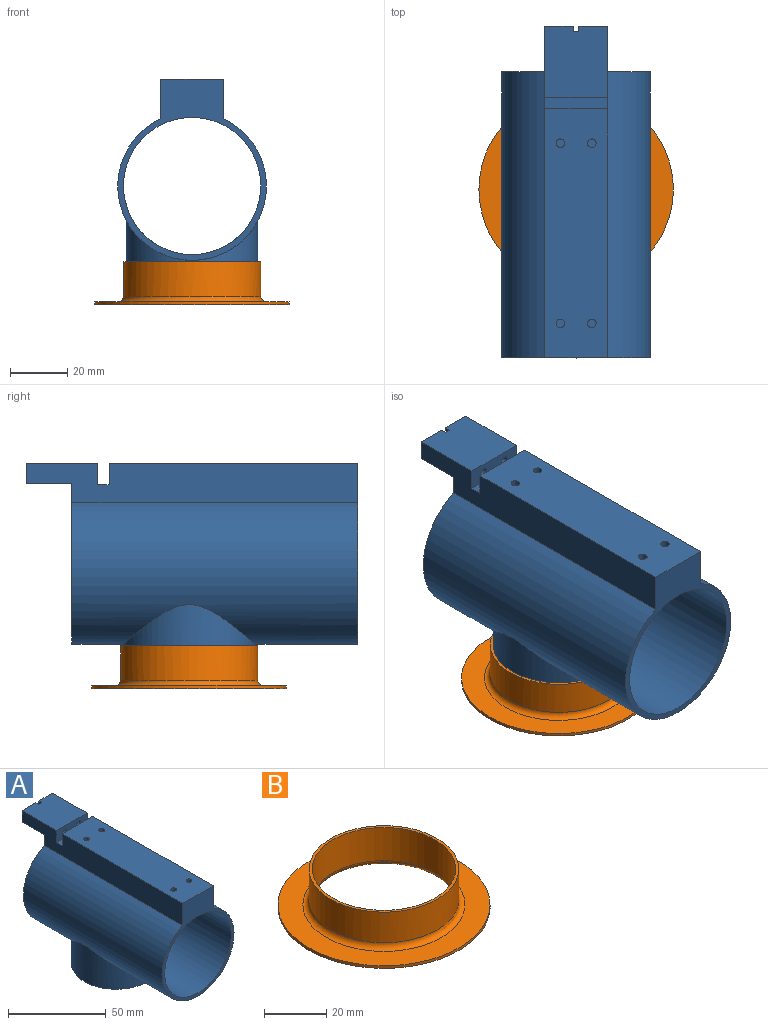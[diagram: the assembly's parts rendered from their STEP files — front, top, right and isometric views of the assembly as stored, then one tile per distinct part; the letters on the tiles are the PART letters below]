
ASSEMBLY  parts=2 mates=1
PART A: 34 faces, bbox 52x116x72.4 mm
  f0: plane 87x22mm, normal (0,0,1), area 1885.7mm2, adj f4,f10,f16,f18,f26,f28,f30,f32
  f1: plane 2.65x0.8mm, normal (0,1,0), area 1.5mm2, adj f2,f28
  f2: cylinder r=1.5mm len=11mm, axis (0,1,0), area 101.8mm2, adj f1,f18,f28
  f3: plane 10x7.14mm, normal (0,1,0), area 64.3mm2, adj f5,f15,f16,f17,f24
  f4: plane 116x13.8mm, normal (1,0,0), area 1464.6mm2, adj f0,f7,f8,f9,f10,f15,f17,f18
  f5: cylinder r=1.5mm len=25mm, axis (0,1,0), area 235.6mm2, adj f3,f19
  f6: cylinder r=1.5mm len=25mm, axis (0,1,0), area 235.6mm2, adj f7,f19
  f7: plane 10x7.14mm, normal (0,1,0), area 64.3mm2, adj f4,f6,f15,f17,f23
  f8: plane 56.22x52mm, normal (0,1,0), area 424.6mm2, adj f4,f9,f11,f16,f17
  f9: cylinder r=26mm len=100mm, axis (0,-1,0), area 12151.7mm2, adj f4,f8,f10,f14,f16
  f10: plane 63.36x52mm, normal (0,-1,0), area 581.6mm2, adj f0,f4,f9,f11,f16
  f11: cylinder r=24mm len=100mm, axis (0,-1,0), area 13296.3mm2, adj f8,f10,f12
  f12: cylinder r=22mm len=44mm, axis (0,0,-1), area 2408.5mm2, adj f11,f13
  f13: plane 46x46mm, normal (0,0,-1), area 141.4mm2, adj f12,f14
  f14: cylinder r=23mm len=46mm, axis (0,0,-1), area 2213.1mm2, adj f9,f13
  f15: plane 25x22mm, normal (0,0,1), area 546mm2, adj f3,f4,f7,f16,f19,f23,f24,f25
  f16: plane 116x13.8mm, normal (-1,0,0), area 1464.6mm2, adj f0,f3,f8,f9,f10,f15,f17,f18
  f17: plane 22x16mm, normal (0,0,-1), area 348mm2, adj f3,f4,f7,f8,f16,f23,f24,f25
  f18: plane 22x7.46mm, normal (0,1,0), area 150mm2, adj f0,f2,f4,f16,f20,f22
  f19: plane 22x7.46mm, normal (0,-1,0), area 150mm2, adj f4,f5,f6,f15,f16,f20
  f20: plane 22x4mm, normal (0,0,1), area 88mm2, adj f4,f16,f18,f19
  f21: plane 2.65x0.8mm, normal (0,1,0), area 1.5mm2, adj f22,f26
  f22: cylinder r=1.5mm len=11mm, axis (0,1,0), area 101.8mm2, adj f18,f21,f26
  f23: plane 7.14x2mm, normal (-1,0,0), area 14.3mm2, adj f7,f15,f17,f25
  f24: plane 7.14x2mm, normal (1,0,0), area 14.3mm2, adj f3,f15,f17,f25
  f25: plane 7.14x2mm, normal (0,1,0), area 14.3mm2, adj f15,f17,f23,f24
  f26: cylinder r=1.5mm len=11mm, axis (0,0,1), area 97.5mm2, adj f0,f21,f22,f27
  f27: plane 3x3mm, normal (0,0,1), area 7.1mm2, adj f26
  f28: cylinder r=1.5mm len=11mm, axis (0,0,1), area 97.5mm2, adj f0,f1,f2,f29
  f29: plane 3x3mm, normal (0,0,1), area 7.1mm2, adj f28
  f30: cylinder r=1.5mm len=11mm, axis (0,0,1), area 103.7mm2, adj f0,f31
  f31: plane 3x3mm, normal (0,0,1), area 7.1mm2, adj f30
  f32: cylinder r=1.5mm len=11mm, axis (0,0,1), area 103.7mm2, adj f0,f33
  f33: plane 3x3mm, normal (0,0,1), area 7.1mm2, adj f32
PART B: 8 faces, bbox 68x68x15 mm
  f0: plane 68x68mm, normal (0,0,1), area 1508mm2, adj f5,f6
  f1: cylinder r=24mm len=48mm, axis (0,0,-1), area 1809.6mm2, adj f2,f6
  f2: plane 48x48mm, normal (0,0,1), area 147.7mm2, adj f1,f3
  f3: cylinder r=23mm len=46mm, axis (0,0,-1), area 1878.7mm2, adj f2,f7
  f4: plane 68x68mm, normal (0,0,-1), area 1668.2mm2, adj f5,f7
  f5: cylinder r=34mm len=68mm, axis (0,0,-1), area 213.6mm2, adj f0,f4
  f6: torus R=26mm, axis (0,0,1), area 488.1mm2, adj f0,f1
  f7: torus R=25mm, axis (0,0,-1), area 468.3mm2, adj f3,f4
PLACE A rot(axis=(0,0,-1),0deg) t=(47.38,-36.51,-87.71)mm
PLACE B rot(axis=(0,0,-1),0deg) t=(47.38,-36.51,-94.26)mm
MATE cylindrical A.f14 <-> B.f1  axis (0,0,-1) through (47.38,-36.51,-76.16)mm
